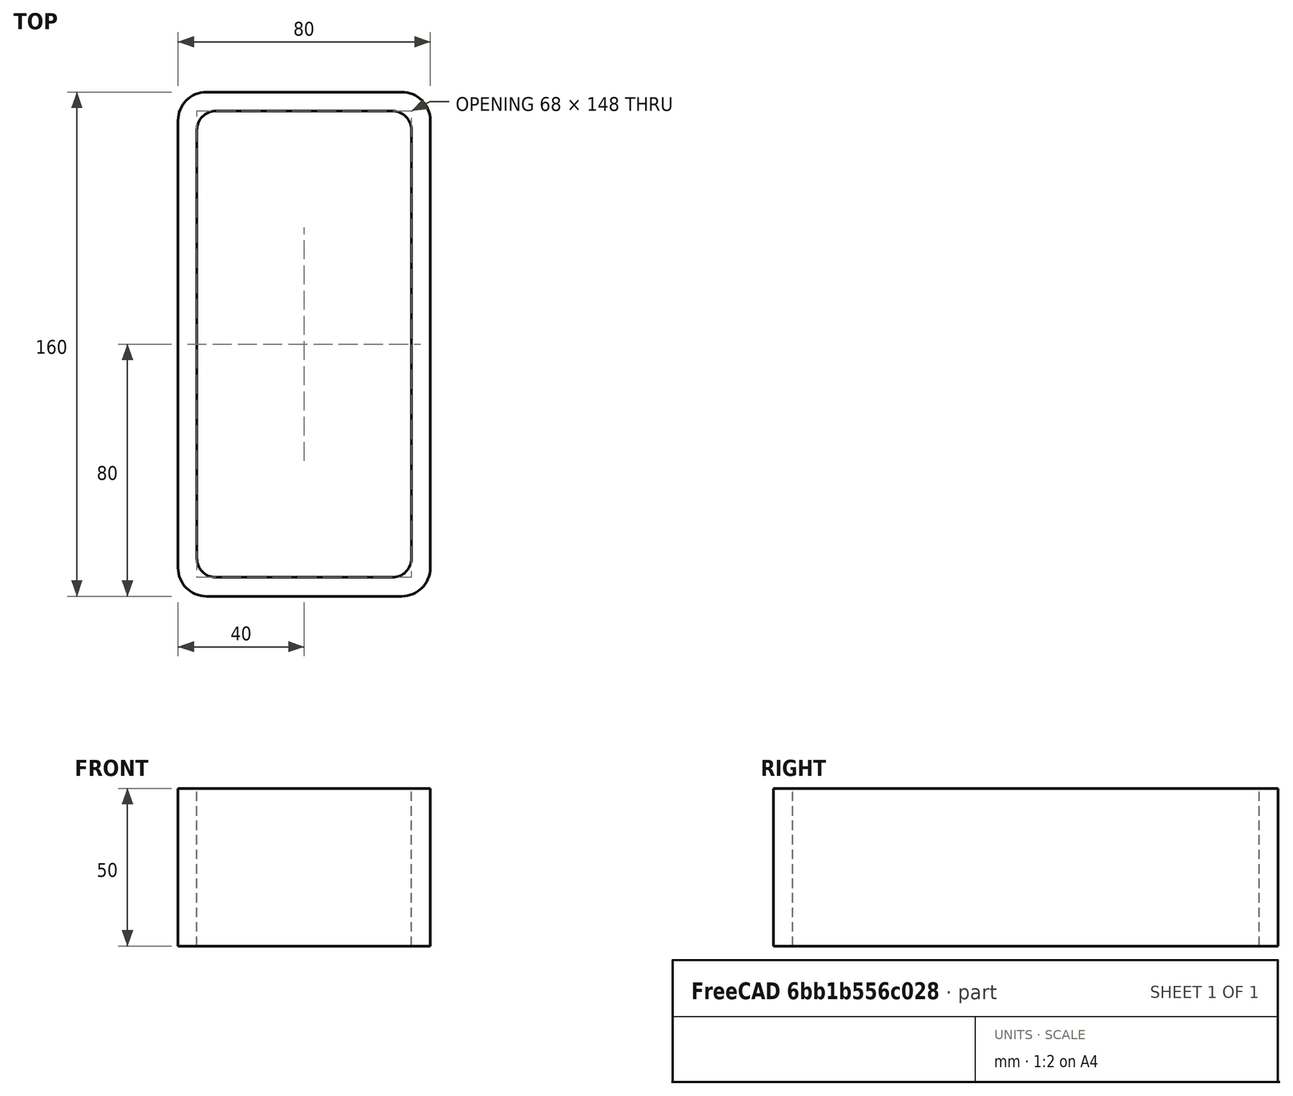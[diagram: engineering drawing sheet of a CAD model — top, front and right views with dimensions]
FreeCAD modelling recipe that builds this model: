
FCSTD DOCUMENT  (FreeCAD 0.15R4671 (Git))
Label: Rectangular hollow section 160x80x6 EN10219 S235JRH
License: All rights reserved
LicenseURL: http://en.wikipedia.org/wiki/All_rights_reserved
objects: Sketcher::SketchObject×1, Part::Extrusion×1
note: 2 computed .brp shape members not serialized (recipe doc carries the construction recipe); baked Part::Feature solids carry a one-line shape summary decoded from their .brp

FEATURE [Sketcher::SketchObject] Sketch
  sketch-geometry (16):
    g0: LineSegment StartX=-28 StartY=74 StartZ=0 EndX=28 EndY=74 EndZ=0
    g1: LineSegment StartX=34 StartY=68 StartZ=0 EndX=34 EndY=-68 EndZ=0
    g2: LineSegment StartX=28 StartY=-74 StartZ=0 EndX=-28 EndY=-74 EndZ=0
    g3: LineSegment StartX=-34 StartY=-68 StartZ=0 EndX=-34 EndY=68 EndZ=0
    g4: LineSegment StartX=-31 StartY=80 StartZ=0 EndX=31 EndY=80 EndZ=0
    g5: LineSegment StartX=40 StartY=71 StartZ=0 EndX=40 EndY=-71 EndZ=0
    g6: LineSegment StartX=31 StartY=-80 StartZ=0 EndX=-31 EndY=-80 EndZ=0
    g7: LineSegment StartX=-40 StartY=-71 StartZ=0 EndX=-40 EndY=71 EndZ=0
    g8: ArcOfCircle CenterX=-28 CenterY=68 CenterZ=0 NormalX=0 NormalY=0 NormalZ=1 Radius=6 StartAngle=1.5708 EndAngle=3.14159
    g9: ArcOfCircle CenterX=28 CenterY=68 CenterZ=0 NormalX=0 NormalY=0 NormalZ=1 Radius=6 StartAngle=0 EndAngle=1.5708
    g10: ArcOfCircle CenterX=28 CenterY=-68 CenterZ=0 NormalX=0 NormalY=0 NormalZ=1 Radius=6 StartAngle=4.71239 EndAngle=6.28319
    g11: ArcOfCircle CenterX=-28 CenterY=-68 CenterZ=0 NormalX=0 NormalY=0 NormalZ=1 Radius=6 StartAngle=3.14159 EndAngle=4.71239
    g12: ArcOfCircle CenterX=31 CenterY=71 CenterZ=0 NormalX=0 NormalY=0 NormalZ=1 Radius=9 StartAngle=0 EndAngle=1.5708
    g13: ArcOfCircle CenterX=31 CenterY=-71 CenterZ=0 NormalX=0 NormalY=0 NormalZ=1 Radius=9 StartAngle=4.71239 EndAngle=6.28319
    g14: ArcOfCircle CenterX=-31 CenterY=-71 CenterZ=0 NormalX=0 NormalY=0 NormalZ=1 Radius=9 StartAngle=3.14159 EndAngle=4.71239
    g15: ArcOfCircle CenterX=-31 CenterY=71 CenterZ=0 NormalX=0 NormalY=0 NormalZ=1 Radius=9 StartAngle=1.5708 EndAngle=3.14159
  constraints (36):
    c: Horizontal(g2)
    c: Vertical(g3)
    c: Horizontal(g6)
    c: Vertical(g7)
    c: Tangent(g3,g8) = 1.5708
    c: Tangent(g0,g8) = 1.5708
    c: Tangent(g0,g9) = 1.5708
    c: Tangent(g1,g9) = 1.5708
    c: Tangent(g1,g10) = 1.5708
    c: Tangent(g2,g10) = 1.5708
    c: Tangent(g2,g11) = 1.5708
    c: Tangent(g3,g11) = 1.5708
    c: Tangent(g4,g12) = 1.5708
    c: Tangent(g5,g12) = 1.5708
    c: Tangent(g5,g13) = 1.5708
    c: Tangent(g6,g13) = 1.5708
    c: Tangent(g6,g14) = 1.5708
    c: Tangent(g7,g14) = 1.5708
    c: Tangent(g7,g15) = 1.5708
    c: Tangent(g4,g15) = 1.5708
    c: Equal(g9,g8)
    c: Equal(g9,g11)
    c: Equal(g9,g10)
    c: Equal(g12,g15)
    c: Equal(g12,g14)
    c: Equal(g12,g13)
    c: Symmetric(g4,g6,g-1)
    c: Symmetric(g7,g5,g-2)
    c: DistanceY(g4,g6) = -160
    c: DistanceX(g7,g5) = 80
    c: Symmetric(g3,g1,g-2)
    c: Symmetric(g0,g2,g-1)
    c: DistanceY(g0,g4) = 6
    c: DistanceX(g5,g1) = -6
    c: Radius(g9) = 6
    c: Radius(g12) = 9
FEATURE [Part::Extrusion] Extrude  label="Rectangular hollow section 160x80x6 EN10219 S235JRH"
  Base = -> Sketch
  Dir = (0,0,50)
  Solid = true
